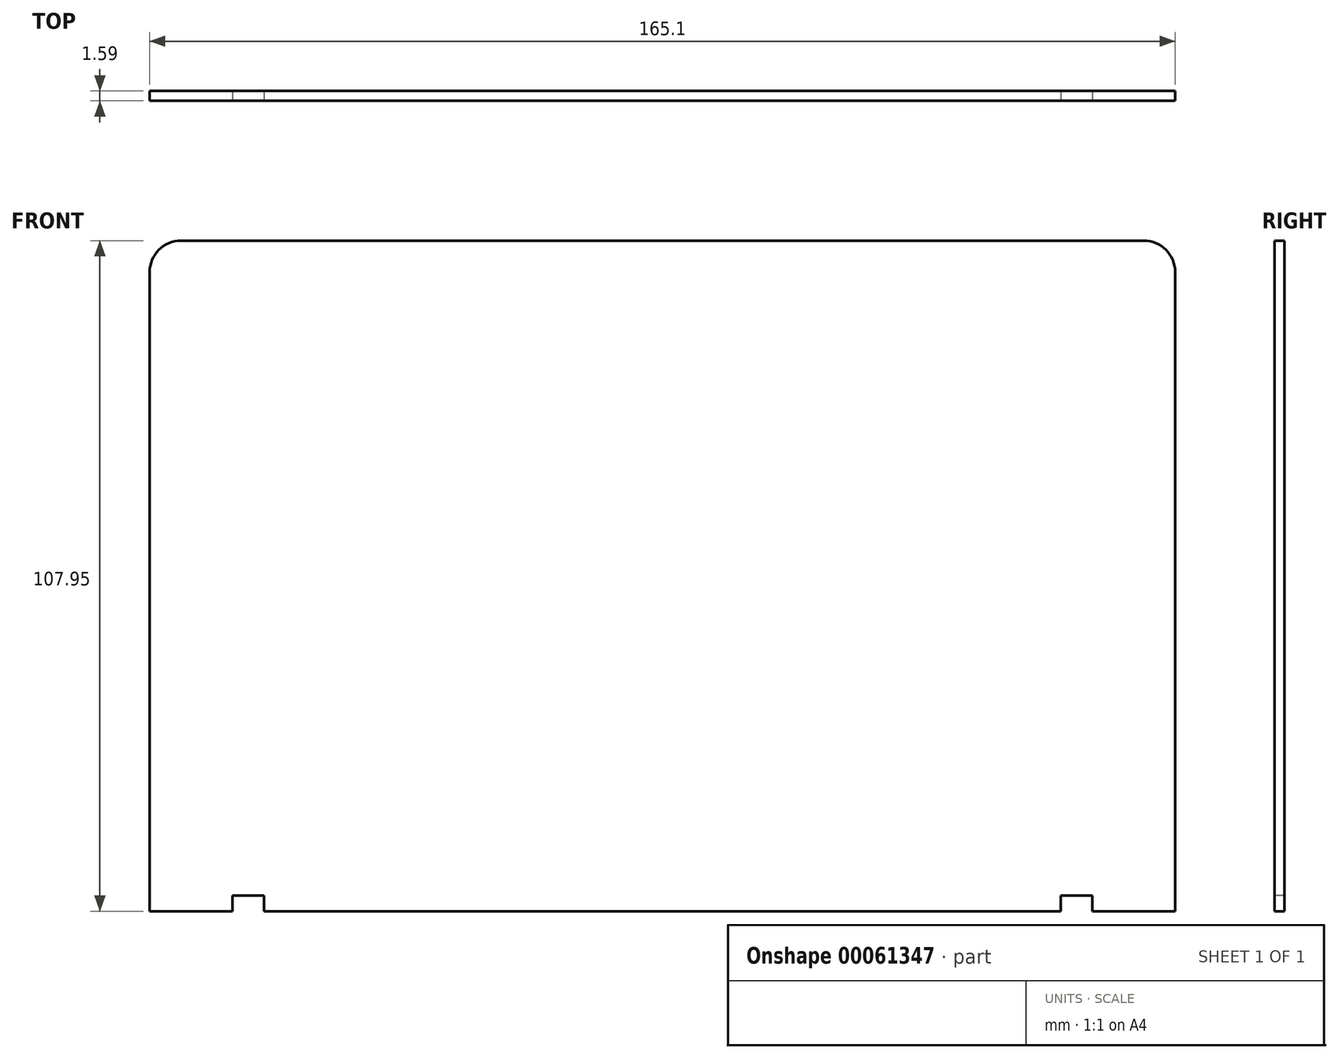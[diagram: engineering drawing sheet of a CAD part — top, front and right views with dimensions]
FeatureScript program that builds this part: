
annotation { "Feature Type Name" : "Feature", "Feature Type Description" : "" }
export const myFeature = defineFeature(function(context is Context, id is Id, definition is map)
    precondition{}
    {
        {
            var Q0;
            Q0=qCreatedBy(makeId("Front.planeOp"),FACE);
            var sketch = newSketch(context, id + "F0", { "sketchPlane" : qUnion([Q0])});
            skLineSegment(sketch, "E0.bottom", {"start": v(-59.54, 91.83) * mm, "end": v(105.56, 91.83) * mm});
            skLineSegment(sketch, "E0.top", {"start": v(-59.54, -16.12) * mm, "end": v(105.56, -16.12) * mm});
            skLineSegment(sketch, "E0.left", {"start": v(-59.54, 91.83) * mm, "end": v(-59.54, -16.12) * mm});
            skLineSegment(sketch, "E0.right", {"start": v(105.56, 91.83) * mm, "end": v(105.56, -16.12) * mm});
            skSolve(sketch);
        }
        {
            var Q0;
            Q0=makeQuery(id+"F0.imprint","IMPRINT",FACE,{"disambiguationData":[TD([[makeQuery(id+"F0.imprint","IMPRINT",EDGE,{"derivedFrom":sQuery(id+"F0.wireOp",EDGE,"E0.bottom")}),-1.0]])]});
            extrude(context, id + "F1", {"entities" : qUnion([Q0]), "depth" : 1.59 * mm});
        }
        {
            var Q0;
            Q0=makeQuery(id+"F1.opExtrude","CAP_FACE",FACE,{"disambiguationData":[OSD([sQuery(id+"F0.wireOp",EDGE,"E0.bottom"),sQuery(id+"F0.wireOp",EDGE,"E0.top"),sQuery(id+"F0.wireOp",EDGE,"E0.left"),sQuery(id+"F0.wireOp",EDGE,"E0.right")])],"isStart":false});
            var sketch = newSketch(context, id + "F2", { "sketchPlane" : qUnion([Q0])});
            skLineSegment(sketch, "E1.bottom", {"start": v(-46.2, -16.12) * mm, "end": v(-41.12, -16.12) * mm});
            skLineSegment(sketch, "E1.top", {"start": v(-46.2, -13.58) * mm, "end": v(-41.12, -13.58) * mm});
            skLineSegment(sketch, "E1.left", {"start": v(-46.2, -16.12) * mm, "end": v(-46.2, -13.58) * mm});
            skLineSegment(sketch, "E1.right", {"start": v(-41.12, -16.12) * mm, "end": v(-41.12, -13.58) * mm});
            skLineSegment(sketch, "E2.bottom", {"start": v(87.15, -16.12) * mm, "end": v(92.23, -16.12) * mm});
            skLineSegment(sketch, "E2.top", {"start": v(87.15, -13.58) * mm, "end": v(92.23, -13.58) * mm});
            skLineSegment(sketch, "E2.left", {"start": v(87.15, -16.12) * mm, "end": v(87.15, -13.58) * mm});
            skLineSegment(sketch, "E2.right", {"start": v(92.23, -16.12) * mm, "end": v(92.23, -13.58) * mm});
            skSolve(sketch);
        }
        {
            var Q0;
            Q0=makeQuery(id+"F2.imprint","IMPRINT",FACE,{"disambiguationData":[TD([[makeQuery(id+"F2.imprint","IMPRINT",EDGE,{"derivedFrom":sQuery(id+"F2.wireOp",EDGE,"E1.bottom")}),1.0]])]});
            var Q1;
            Q1=makeQuery(id+"F2.imprint","IMPRINT",FACE,{"disambiguationData":[TD([[makeQuery(id+"F2.imprint","IMPRINT",EDGE,{"derivedFrom":sQuery(id+"F2.wireOp",EDGE,"E2.bottom")}),1.0]])]});
            extrude(context, id + "F3", {"entities" : qUnion([Q0, Q1]), "operationType" : NewBodyOperationType.REMOVE, "oppositeDirection" : true, "depth" : 25.4 * mm});
        }
        {
            var Q0;
            Q0=makeQuery(id+"F1.opExtrude","SWEPT_EDGE",EDGE,{"disambiguationData":[OSD([sQuery(id+"F0.wireOp",EDGE,"E0.bottom"),sQuery(id+"F0.wireOp",EDGE,"E0.right")])]});
            var Q1;
            Q1=makeQuery(id+"F1.opExtrude","SWEPT_EDGE",EDGE,{"disambiguationData":[OSD([sQuery(id+"F0.wireOp",EDGE,"E0.bottom"),sQuery(id+"F0.wireOp",EDGE,"E0.left")])]});
            fillet(context, id + "F4", {"entities" : qUnion([Q0, Q1]), "radius" : 5.08 * mm, "tangentPropagation" : true, "allowEdgeOverflow" : false});
        }
    });
